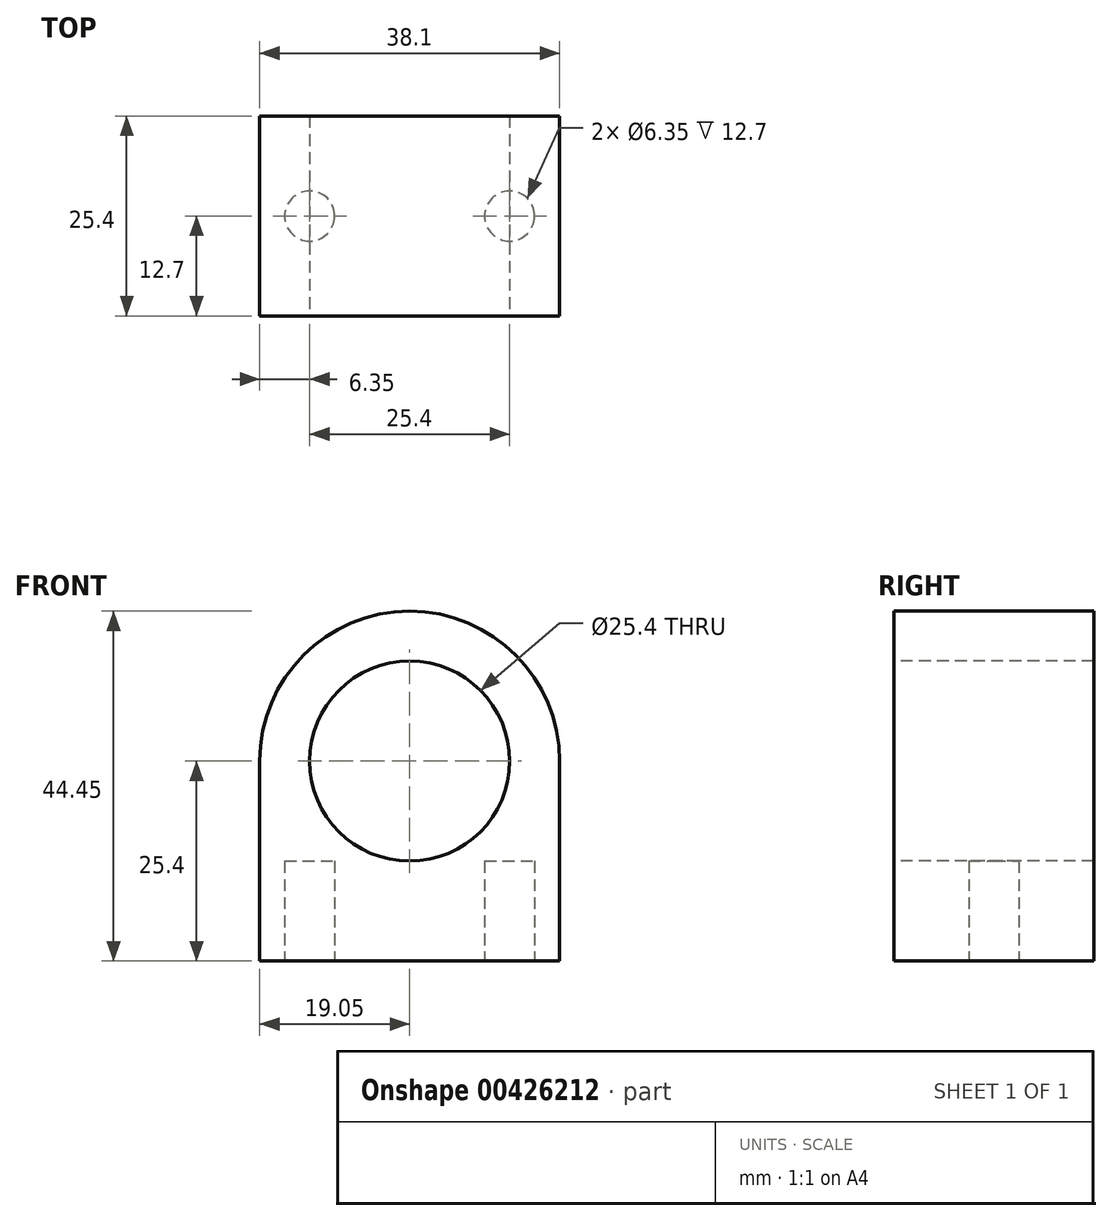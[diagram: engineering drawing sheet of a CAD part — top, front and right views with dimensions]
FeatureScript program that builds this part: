
annotation { "Feature Type Name" : "Feature", "Feature Type Description" : "" }
export const myFeature = defineFeature(function(context is Context, id is Id, definition is map)
    precondition{}
    {
        {
            var Q0;
            Q0=qCreatedBy(makeId("Front.planeOp"),FACE);
            var sketch = newSketch(context, id + "F0", { "sketchPlane" : qUnion([Q0])});
            skLineSegment(sketch, "E0.bottom", {"start": v(0, 0) * mm, "end": v(38.1, 0) * mm});
            skLineSegment(sketch, "E0.top", {"start": v(0, 44.45) * mm, "end": v(38.1, 44.45) * mm});
            skLineSegment(sketch, "E0.left", {"start": v(0, 0) * mm, "end": v(0, 44.45) * mm});
            skLineSegment(sketch, "E0.right", {"start": v(38.1, 0) * mm, "end": v(38.1, 44.45) * mm});
            skSolve(sketch);
        }
        {
            var Q0;
            Q0 = qSketchRegion(id + "F0", true);
            extrude(context, id + "F1", {"entities" : qUnion([Q0]), "depth" : 25.4 * mm});
        }
        {
            var Q0;
            Q0=makeQuery(id+"F1.opExtrude","SWEPT_EDGE",EDGE,{"disambiguationData":[OSD([sQuery(id+"F0.wireOp",EDGE,"E0.top"),sQuery(id+"F0.wireOp",EDGE,"E0.left")])]});
            var Q1;
            Q1=makeQuery(id+"F1.opExtrude","SWEPT_EDGE",EDGE,{"disambiguationData":[OSD([sQuery(id+"F0.wireOp",EDGE,"E0.top"),sQuery(id+"F0.wireOp",EDGE,"E0.right")])]});
            fillet(context, id + "F2", {"entities" : qUnion([Q0, Q1]), "radius" : 19.05 * mm, "tangentPropagation" : true, "allowEdgeOverflow" : false});
        }
        {
            var Q0;
            Q0=makeQuery(id+"F1.opExtrude","CAP_FACE",FACE,{"disambiguationData":[OSD([sQuery(id+"F0.wireOp",EDGE,"E0.bottom"),sQuery(id+"F0.wireOp",EDGE,"E0.top"),sQuery(id+"F0.wireOp",EDGE,"E0.left"),sQuery(id+"F0.wireOp",EDGE,"E0.right")])],"isStart":false});
            var sketch = newSketch(context, id + "F3", { "sketchPlane" : qUnion([Q0])});
            skCircle(sketch, "E1", {"center": v(19.05, 25.4) * mm, "radius": 12.7 * mm});
            skSolve(sketch);
        }
        {
            var Q0;
            Q0 = qSketchRegion(id + "F3", true);
            extrude(context, id + "F4", {"entities" : qUnion([Q0]), "operationType" : NewBodyOperationType.REMOVE, "endBound" : BoundingType.THROUGH_ALL, "oppositeDirection" : true, "depth" : 25.4 * mm});
        }
        {
            var Q0;
            Q0=makeQuery(id+"F1.opExtrude","SWEPT_FACE",FACE,{"disambiguationData":[OSD([sQuery(id+"F0.wireOp",EDGE,"E0.bottom")])]});
            var sketch = newSketch(context, id + "F5", { "sketchPlane" : qUnion([Q0])});
            skCircle(sketch, "E2", {"center": v(6.35, 12.7) * mm, "radius": 3.18 * mm});
            skCircle(sketch, "E3", {"center": v(31.75, 12.7) * mm, "radius": 3.18 * mm});
            skSolve(sketch);
        }
        {
            var Q0;
            Q0 = qSketchRegion(id + "F5", true);
            extrude(context, id + "F6", {"entities" : qUnion([Q0]), "operationType" : NewBodyOperationType.REMOVE, "oppositeDirection" : true, "depth" : 12.7 * mm});
        }
    });
